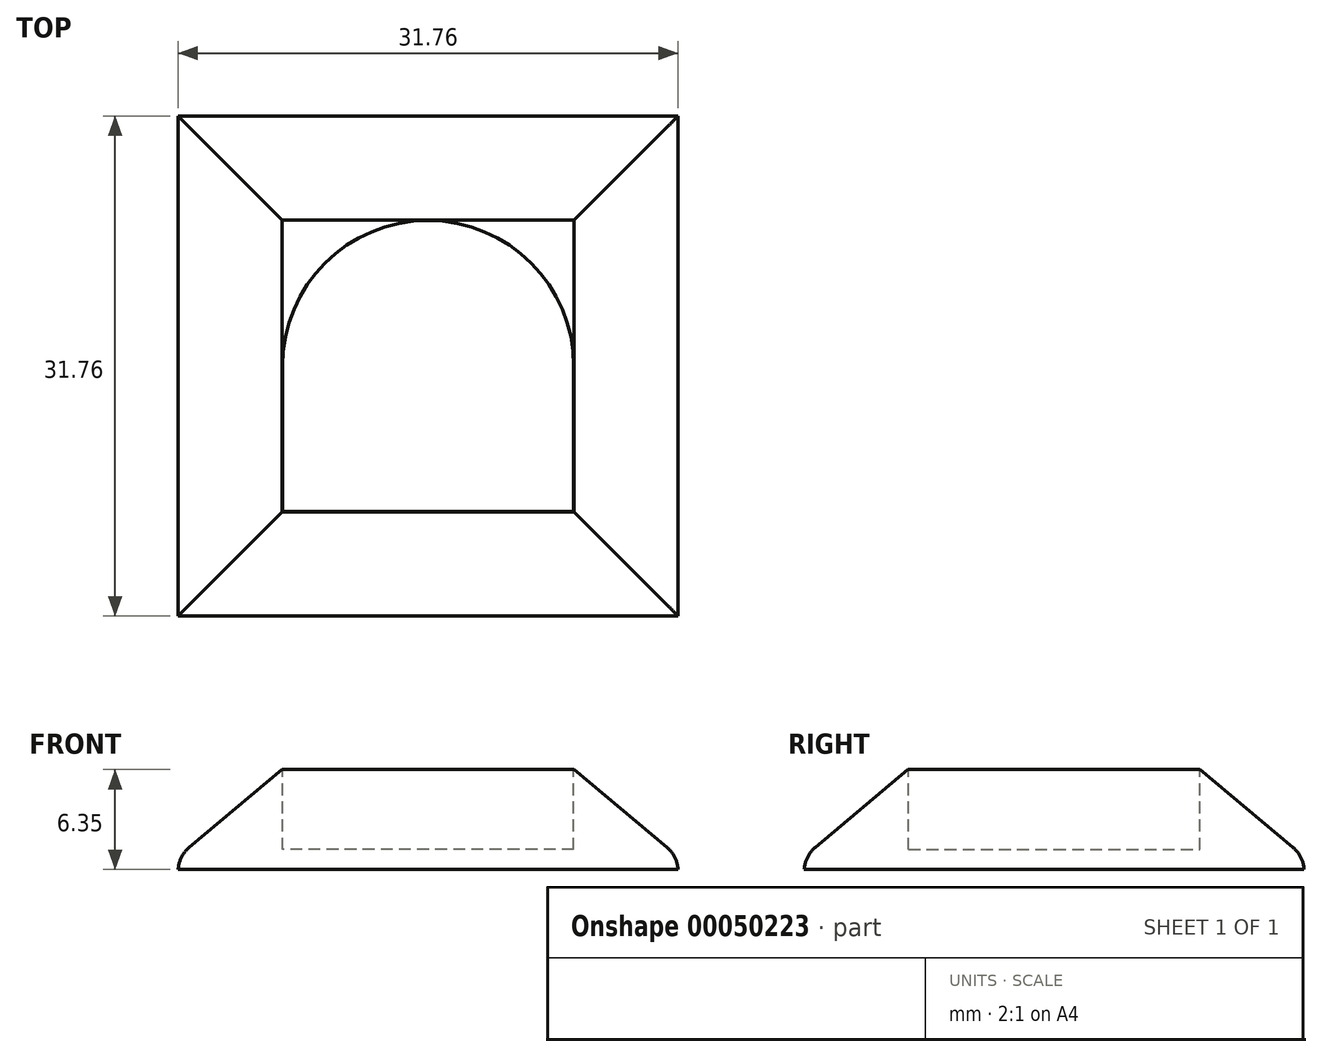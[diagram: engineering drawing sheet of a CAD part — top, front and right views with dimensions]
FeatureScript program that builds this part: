
annotation { "Feature Type Name" : "Feature", "Feature Type Description" : "" }
export const myFeature = defineFeature(function(context is Context, id is Id, definition is map)
    precondition{}
    {
        {
            var Q0;
            Q0=qCreatedBy(makeId("Top.planeOp"),FACE);
            var sketch = newSketch(context, id + "F0", { "sketchPlane" : qUnion([Q0])});
            skLineSegment(sketch, "E0.bottom", {"start": v(15.87, 15.88) * mm, "end": v(-15.88, 15.88) * mm});
            skLineSegment(sketch, "E0.top", {"start": v(15.88, -15.88) * mm, "end": v(-15.87, -15.88) * mm});
            skLineSegment(sketch, "E0.left", {"start": v(15.87, 15.88) * mm, "end": v(15.88, -15.88) * mm});
            skLineSegment(sketch, "E0.right", {"start": v(-15.88, 15.88) * mm, "end": v(-15.87, -15.88) * mm});
            skPoint(sketch, "E0.middle", {"position": v(0, 0) * mm});
            skSolve(sketch);
        }
        {
            var Q0;
            Q0 = qSketchRegion(id + "F0", true);
            extrude(context, id + "F1", {"entities" : qUnion([Q0]), "depth" : 6.35 * mm});
        }
        {
            var Q0;
            Q0=makeQuery(id+"F1.opExtrude","CAP_EDGE",EDGE,{"disambiguationData":[OSD([sQuery(id+"F0.wireOp",EDGE,"E0.right")])],"isStart":false});
            var Q1;
            Q1=makeQuery(id+"F1.opExtrude","CAP_EDGE",EDGE,{"disambiguationData":[OSD([sQuery(id+"F0.wireOp",EDGE,"E0.top")])],"isStart":false});
            var Q2;
            Q2=makeQuery(id+"F1.opExtrude","CAP_EDGE",EDGE,{"disambiguationData":[OSD([sQuery(id+"F0.wireOp",EDGE,"E0.left")])],"isStart":false});
            var Q3;
            Q3=makeQuery(id+"F1.opExtrude","CAP_EDGE",EDGE,{"disambiguationData":[OSD([sQuery(id+"F0.wireOp",EDGE,"E0.bottom")])],"isStart":false});
            chamfer(context, id + "F2", {"entities" : qUnion([Q0, Q1, Q2, Q3]), "chamferType" : ChamferType.OFFSET_ANGLE, "width" : 6.6 * mm, "oppositeDirection" : false, "angle" : 40 * degree, "tangentPropagation" : true});
        }
        {
            var Q0;
            Q0=makeQuery(id+"F1.opExtrude","CAP_FACE",FACE,{"disambiguationData":[OSD([sQuery(id+"F0.wireOp",EDGE,"E0.bottom"),sQuery(id+"F0.wireOp",EDGE,"E0.top"),sQuery(id+"F0.wireOp",EDGE,"E0.left"),sQuery(id+"F0.wireOp",EDGE,"E0.right")])],"isStart":false});
            var sketch = newSketch(context, id + "F3", { "sketchPlane" : qUnion([Q0])});
            skArc(sketch, "E1", {"start": v(9.25, 0) * mm, "mid": v(0, 9.25) * mm, "end": v(-9.25, 0) * mm});
            skLineSegment(sketch, "E2.bottom", {"start": v(9.25, -9.25) * mm, "end": v(-9.25, -9.25) * mm});
            skLineSegment(sketch, "E2.left", {"start": v(9.25, -9.25) * mm, "end": v(9.25, 0) * mm});
            skLineSegment(sketch, "E2.right", {"start": v(-9.25, -9.25) * mm, "end": v(-9.25, 0) * mm});
            skSolve(sketch);
        }
        {
            var Q0;
            Q0=makeQuery(id+"F3.imprint","IMPRINT",FACE,{"disambiguationData":[TD([[makeQuery(id+"F3.imprint","IMPRINT",EDGE,{"derivedFrom":sQuery(id+"F3.wireOp",EDGE,"E1")}),1.0]])]});
            extrude(context, id + "F4", {"entities" : qUnion([Q0]), "operationType" : NewBodyOperationType.REMOVE, "oppositeDirection" : true, "depth" : 5.08 * mm});
        }
        {
            var Q0;
            {var subQ0=sQuery(id+"F0.wireOp",EDGE,"E0.top");Q0=makeQuery(id+"F2.opChamfer","BLEND_EDGE",EDGE,{"blendedFrom":[makeQuery(id+"F1.opExtrude","CAP_EDGE",EDGE,{"disambiguationData":[OSD([subQ0])],"isStart":false}),makeQuery(id+"F1.opExtrude","SWEPT_FACE",FACE,{"disambiguationData":[OSD([subQ0])]})],"blendedInto":[makeQuery(id+"F1.opExtrude","SWEPT_FACE",FACE,{"disambiguationData":[OSD([subQ0])]})]});}
            var Q1;
            {var subQ0=sQuery(id+"F0.wireOp",EDGE,"E0.left");Q1=makeQuery(id+"F2.opChamfer","BLEND_EDGE",EDGE,{"blendedFrom":[makeQuery(id+"F1.opExtrude","CAP_EDGE",EDGE,{"disambiguationData":[OSD([subQ0])],"isStart":false}),makeQuery(id+"F1.opExtrude","SWEPT_FACE",FACE,{"disambiguationData":[OSD([subQ0])]})],"blendedInto":[makeQuery(id+"F1.opExtrude","SWEPT_FACE",FACE,{"disambiguationData":[OSD([subQ0])]})]});}
            var Q2;
            {var subQ0=sQuery(id+"F0.wireOp",EDGE,"E0.right");Q2=makeQuery(id+"F2.opChamfer","BLEND_EDGE",EDGE,{"blendedFrom":[makeQuery(id+"F1.opExtrude","CAP_EDGE",EDGE,{"disambiguationData":[OSD([subQ0])],"isStart":false}),makeQuery(id+"F1.opExtrude","SWEPT_FACE",FACE,{"disambiguationData":[OSD([subQ0])]})],"blendedInto":[makeQuery(id+"F1.opExtrude","SWEPT_FACE",FACE,{"disambiguationData":[OSD([subQ0])]})]});}
            var Q3;
            {var subQ0=sQuery(id+"F0.wireOp",EDGE,"E0.bottom");Q3=makeQuery(id+"F2.opChamfer","BLEND_EDGE",EDGE,{"blendedFrom":[makeQuery(id+"F1.opExtrude","CAP_EDGE",EDGE,{"disambiguationData":[OSD([subQ0])],"isStart":false}),makeQuery(id+"F1.opExtrude","SWEPT_FACE",FACE,{"disambiguationData":[OSD([subQ0])]})],"blendedInto":[makeQuery(id+"F1.opExtrude","SWEPT_FACE",FACE,{"disambiguationData":[OSD([subQ0])]})]});}
            fillet(context, id + "F5", {"entities" : qUnion([Q0, Q1, Q2, Q3]), "radius" : 2 * mm, "tangentPropagation" : true, "allowEdgeOverflow" : false});
        }
    });
